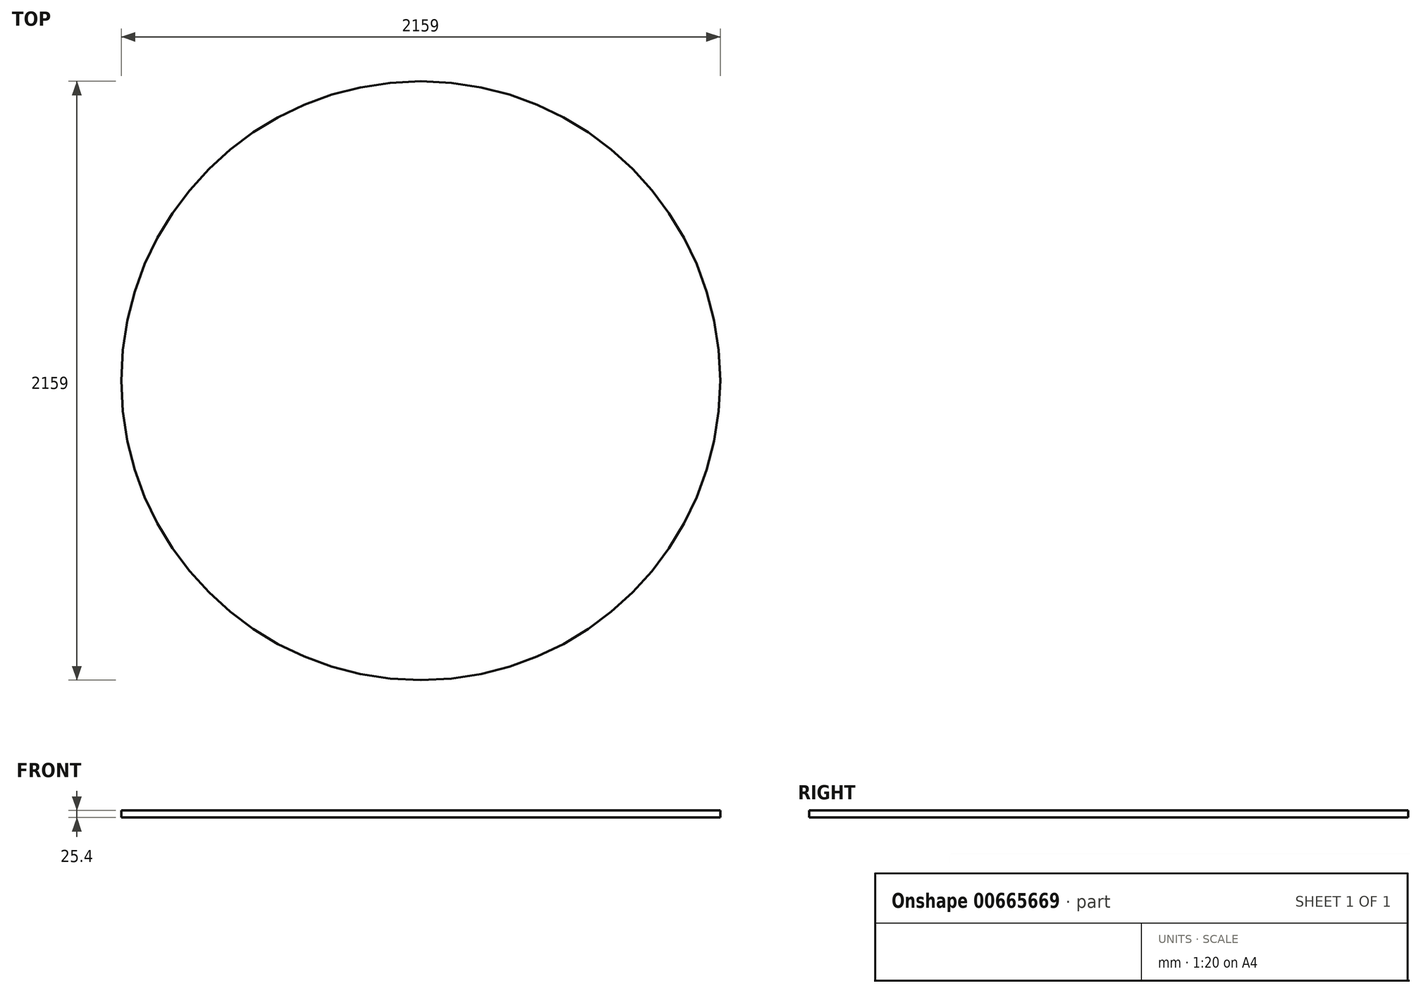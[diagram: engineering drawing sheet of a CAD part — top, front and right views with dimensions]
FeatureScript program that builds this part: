
annotation { "Feature Type Name" : "Feature", "Feature Type Description" : "" }
export const myFeature = defineFeature(function(context is Context, id is Id, definition is map)
    precondition{}
    {
        {
            var Q0;
            Q0=qCreatedBy(makeId("Top.planeOp"),FACE);
            var sketch = newSketch(context, id + "F0", { "sketchPlane" : qUnion([Q0])});
            skCircle(sketch, "E0", {"center": v(0, 0) * mm, "radius": 1079.5 * mm});
            skSolve(sketch);
        }
        {
            var Q0;
            Q0 = qSketchRegion(id + "F0", true);
            extrude(context, id + "F1", {"entities" : qUnion([Q0]), "depth" : 25.4 * mm, "offsetDistance" : 25.4 * mm});
        }
    });
